# Revit family: Mezcladora de lavabo EP-2006
name_source: partatom
category: Aparatos sanitarios
revit_build: Autodesk Revit 2016 (Build: 20150220_1215(x64)
units: mm (PartAtom-declared; Revit-internal decimal feet)

## family parameters
Compartido = Sí
Corte con vacíos al cargar = No
Cota de conector redondo = Diámetro de uso
Número OmniClass = 23.45.55.17
Punto de cálculo de habitación = Sí
Se basa en plano de trabajo = Sí
Siempre vertical = Sí
Tipo de pieza = Normal
Título OmniClass = Mixing Faucets

## types (1)
- EP-2006
    Chrome = Brass Chromed
    Comentarios de tipo = Lavatory Faucet Assemblies
    Conexión AC = Sí
    Conexión AF = Sí
    Descripción = 12" Nuva Widespread Faucet Assembly Pop-up Drain
    Documentation = http://www.helvex.com.mx
    Elevación por defecto = 1"
    Fabricante = Helvex
    Features = ¼ Left Turn and Right Turn Val-vex Ceramic Disc, Setting Tool Included For 8", 10" and 12" Installation, Hidden Aerator
    Imagen de tipo = EP-2006.JPG
    Inlet Threads = ½" - 14 NPSM
    Instructive = http://www.helvex.com.mx
    Max. Working Pressure = 85.3 psi
    Mechanical Guide = http://www.helvex.com.mx
    Min. Working Pressure = 2.9 psi
    Modelo = EP-2006
    Niquel Duravex = Niquel Duravex
    Satin = Brass Satín
    Total Height = 4"
    Total Length = 7"
    URL = http://www.helvex.com.mx

## geometry (parser evidence)
native form markers: Sweep x3
no freeform markers — native parametric forms only
